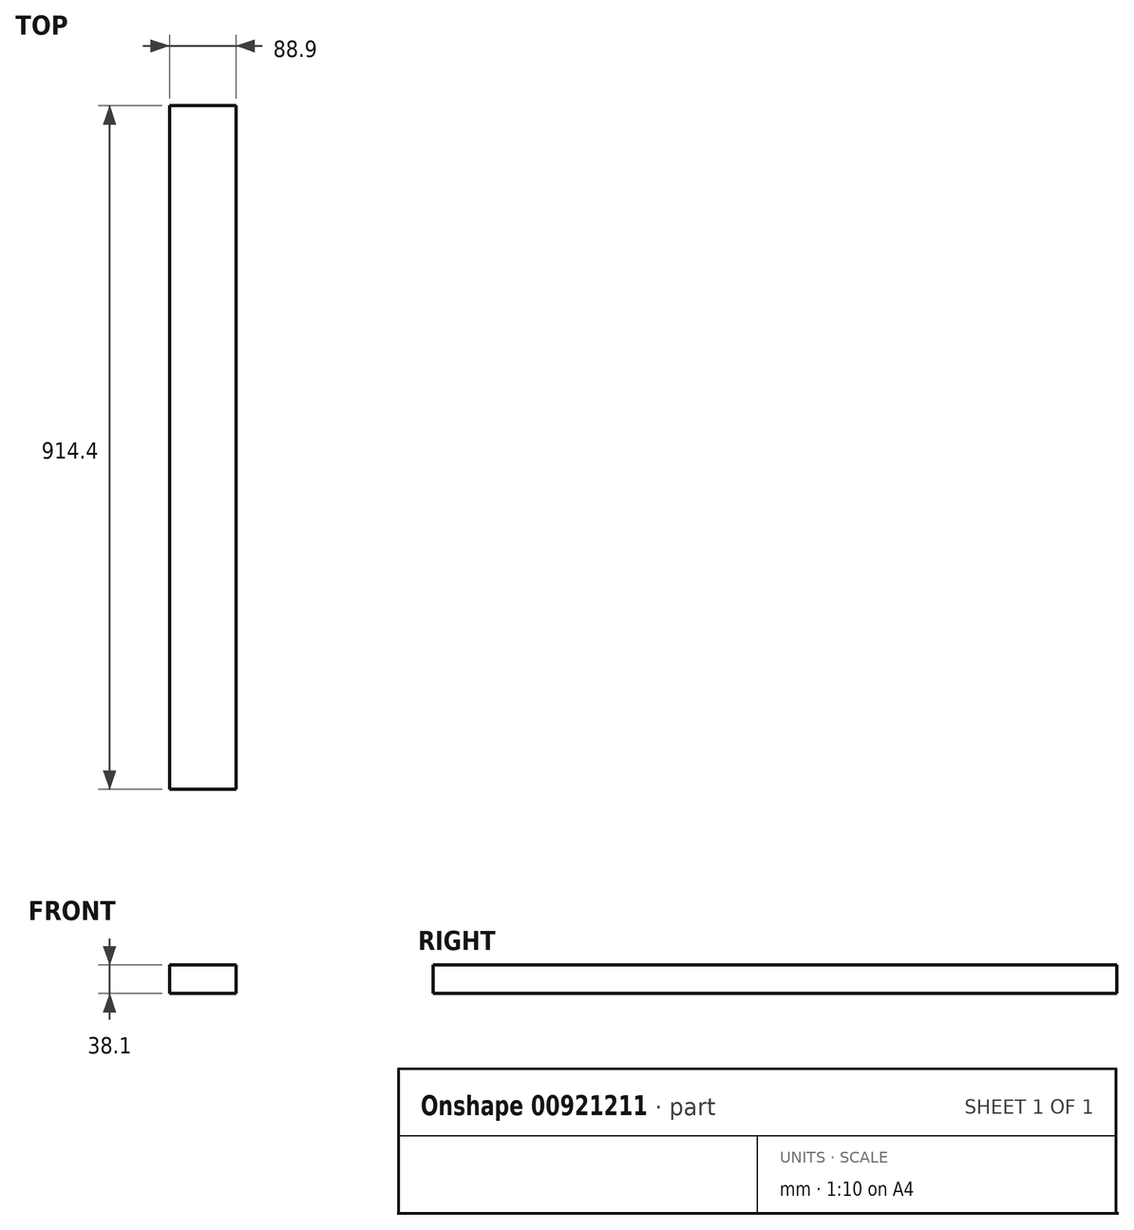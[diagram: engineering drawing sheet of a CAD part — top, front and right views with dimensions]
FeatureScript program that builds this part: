
annotation { "Feature Type Name" : "Feature", "Feature Type Description" : "" }
export const myFeature = defineFeature(function(context is Context, id is Id, definition is map)
    precondition{}
    {
        {
            var Q0;
            Q0=qCreatedBy(makeId("Front.planeOp"),FACE);
            var sketch = newSketch(context, id + "F0", { "sketchPlane" : qUnion([Q0])});
            skLineSegment(sketch, "E0.bottom", {"start": v(-44.45, 19.05) * mm, "end": v(44.45, 19.05) * mm});
            skLineSegment(sketch, "E0.top", {"start": v(-44.45, -19.05) * mm, "end": v(44.45, -19.05) * mm});
            skLineSegment(sketch, "E0.left", {"start": v(-44.45, 19.05) * mm, "end": v(-44.45, -19.05) * mm});
            skLineSegment(sketch, "E0.right", {"start": v(44.45, 19.05) * mm, "end": v(44.45, -19.05) * mm});
            skPoint(sketch, "E0.middle", {"position": v(0, 0) * mm});
            skSolve(sketch);
        }
        {
            var Q0;
            Q0 = qSketchRegion(id + "F0", true);
            extrude(context, id + "F1", {"entities" : qUnion([Q0]), "endBound" : BoundingType.SYMMETRIC, "depth" : 914.4 * mm, "offsetDistance" : 25.4 * mm});
        }
    });
